# Revit family: Sink_Dual_Mounted-American_Standard-Edgewater-18SB.9252211.075
name_source: partatom
category: Plumbing Fixtures
units: mm (PartAtom-declared; Revit-internal decimal feet)

## family parameters
Always vertical = No
Cut with Voids When Loaded = Yes
OmniClass Number = 23.45.05.14.14
OmniClass Title = Sinks/Lavatories
Part Type = Normal
Room Calculation Point = No
Round Connector Dimension = Use Diameter
Shared = Yes
Work Plane-Based = Yes

## types (1)
- 18SB.9252211.075
    ASME A112.19.3 = Yes
    Assembly Code = D2010410
    Basin Shape = Rectangular
    Bottom Grid = Yes
    CW Connection = Yes
    CWFU = 2
    Cold Water Connection Diameter = 1/2"
    Cold Water Connection Height = 20"
    Cold Water Connection Radius = 1/4"
    Cold Water Connection Width = 4"
    Cutout Template = Yes
    Default Elevation = 34"
    Description = Edgewater 25 x 22 Single Bowl Stainless Steel Kitchen Sink
    Finish = Stainless Steel-American Standard-075-Satin
    HW Connection = Yes
    HWFU = 2
    Height = 9"
    Hot Water Connection Diameter = 1"
    Hot Water Connection Height = 20"
    Hot Water Connection Radius = 1/4"
    Hot Water Connection Width = 4"
    Installation Type = Top Mount
    Length = 25"
    Manufacturer = American Standard
    Material = Stainless Steel-American Standard-075-Satin
    Model = 18SB.9252211.075
    Price = Prices may vary. Please consult Manufacturer Representative for most up-to-date price list.
    Product Documentation Link = https://americanstandard.box.com
    Product Page URL = https://www.americanstandard-us.com
    Revised Date = 01/10/2022
    Top Mount = Yes
    Top Mount Sink Clips = Yes
    URL = https://www.americanstandard-us.com
    Under Mount = No
    Under Mount Sink Clips = Yes
    Vent Connection = No
    WFU = 3
    Wall Distance = 1"
    Warranty Information = Limited Lifetime Warranty
    Waste Connection = Yes
    Waste Connection Diameter = 1 1/2"
    Waste Connection Height = 18"
    Waste Connection Radius = 3/4"
    Waste Fitting = Yes
    Width = 22"

## geometry (parser evidence)
native form markers: Sweep x2
no freeform markers — native parametric forms only
